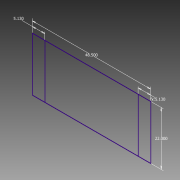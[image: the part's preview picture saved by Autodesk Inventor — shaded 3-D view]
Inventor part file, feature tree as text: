
AUTODESK INVENTOR PART (.ipt)
format: ipt  version: 2013 (Build 170138000, 138)  size: 65,024 bytes
history: native  units: in
note: dims shown in document units (in); Inventor stores cm internally (conversion verified against a paired STEP export)
features: sketch x1
ambient origin geometry x8: Origin, YZ Plane, XZ Plane, XY Plane, X Axis, Y Axis, Z Axis, Center Point
feature tree (1):
  sketch  "Sketch1"  dims[d2=48.5in d3=22.0in d4=5.13in d5=5.13in]
